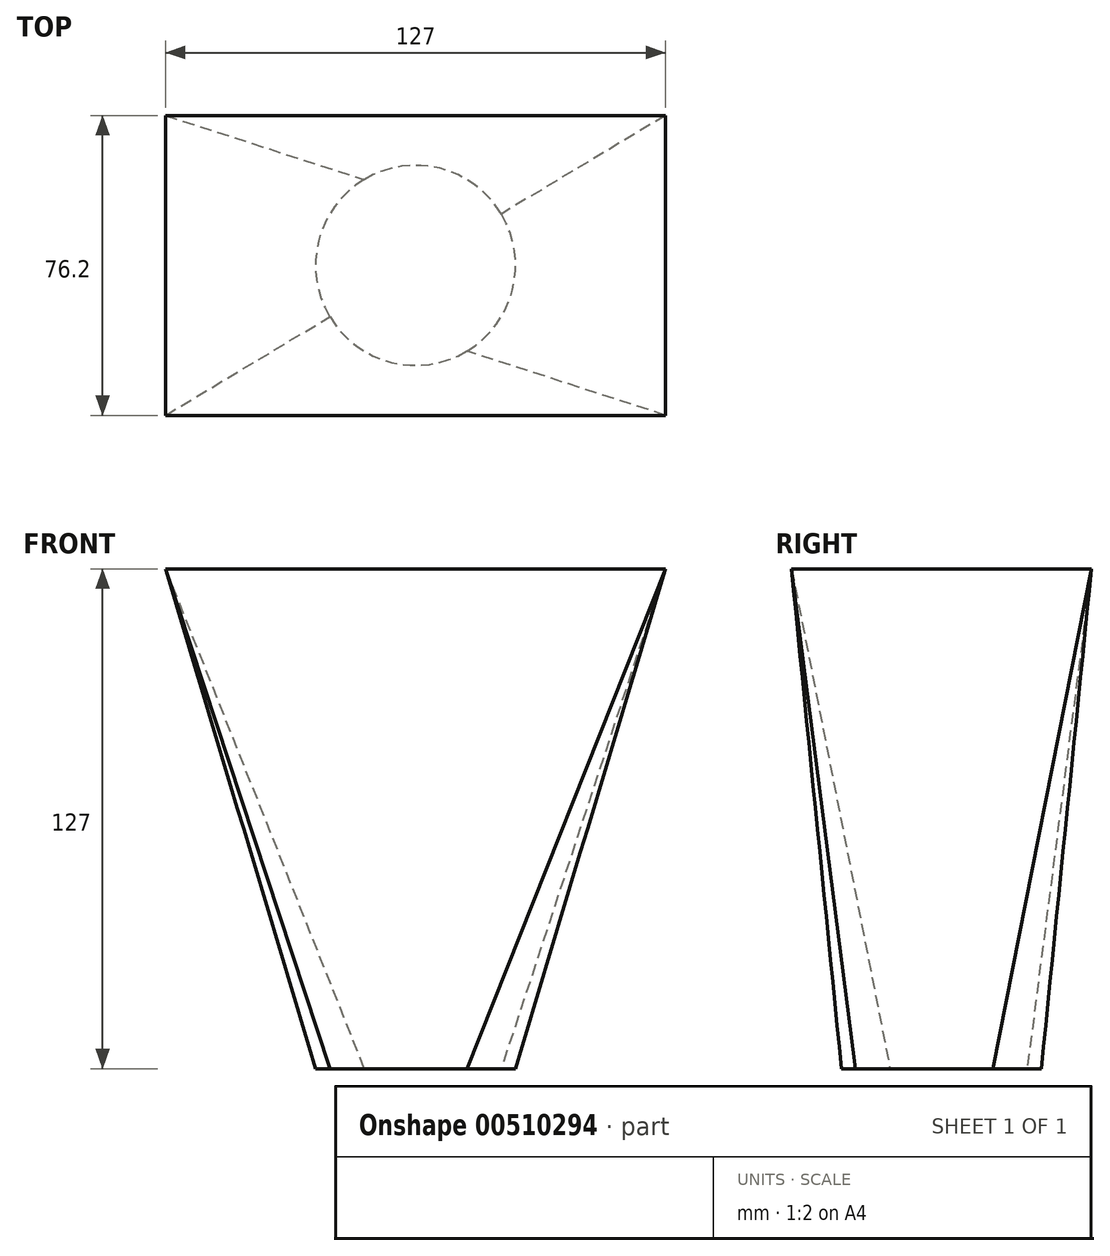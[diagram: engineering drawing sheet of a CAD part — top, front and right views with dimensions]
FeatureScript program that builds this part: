
annotation { "Feature Type Name" : "Feature", "Feature Type Description" : "" }
export const myFeature = defineFeature(function(context is Context, id is Id, definition is map)
    precondition{}
    {
        {
            var Q0;
            Q0=qCreatedBy(makeId("Top.planeOp"),FACE);
            var sketch = newSketch(context, id + "F0", { "sketchPlane" : qUnion([Q0])});
            skCircle(sketch, "E0", {"center": v(0, 0) * mm, "radius": 25.4 * mm});
            skSolve(sketch);
        }
        {
            var Q0;
            Q0=qCreatedBy(makeId("Top.planeOp"),FACE);
            cPlane(context, id + "F1", {"entities" : qUnion([Q0]), "cplaneType" : CPlaneType.OFFSET, "offset" : 127 * mm, "width" : 152.4 * mm, "height" : 152.4 * mm});
        }
        {
            var Q0;
            Q0=qCreatedBy(id+"F1.planeOp",FACE);
            var sketch = newSketch(context, id + "F2", { "sketchPlane" : qUnion([Q0])});
            skLineSegment(sketch, "E1.bottom", {"start": v(63.5, 38.1) * mm, "end": v(-63.5, 38.1) * mm});
            skLineSegment(sketch, "E1.top", {"start": v(63.5, -38.1) * mm, "end": v(-63.5, -38.1) * mm});
            skLineSegment(sketch, "E1.left", {"start": v(63.5, 38.1) * mm, "end": v(63.5, -38.1) * mm});
            skLineSegment(sketch, "E1.right", {"start": v(-63.5, 38.1) * mm, "end": v(-63.5, -38.1) * mm});
            skPoint(sketch, "E1.middle", {"position": v(0, 0) * mm});
            skSolve(sketch);
        }
        {
            var Q0;
            Q0=makeQuery(id+"F2.imprint","IMPRINT",FACE,{"disambiguationData":[TD([[makeQuery(id+"F2.imprint","IMPRINT",EDGE,{"derivedFrom":sQuery(id+"F2.wireOp",EDGE,"E1.bottom")}),1.0]])]});
            var Q1;
            Q1=makeQuery(id+"F0.imprint","IMPRINT",FACE,{"disambiguationData":[TD([[makeQuery(id+"F0.imprint","IMPRINT",EDGE,{"derivedFrom":sQuery(id+"F0.wireOp",EDGE,"E0")}),1.0]])]});
            loft(context, id + "F3", {"sheetProfilesArray" : [{ "sheetProfileEntities" : qUnion([Q0]) }, { "sheetProfileEntities" : qUnion([Q1]) }]});
        }
    });
